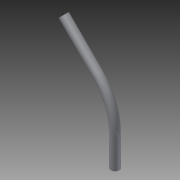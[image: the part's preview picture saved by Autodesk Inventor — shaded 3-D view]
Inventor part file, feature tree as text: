
AUTODESK INVENTOR PART (.ipt)
format: ipt  version: 2014 SP1 (Build 180222100, 222)  size: 117,248 bytes
history: native  units: in
note: dims shown in document units (in); Inventor stores cm internally (conversion verified against a paired STEP export)
features: reference x5, sketch x2, plane x2, sweep x1
ambient origin geometry x8: Origin, YZ Plane, XZ Plane, XY Plane, X Axis, Y Axis, Z Axis, Center Point
bodies: Solid1 (feature_tree)
feature tree (10):
  sketch  "Sketch1"  dims[d0=0.7274in d1=0.7274in]
  plane  "Work Plane2"
  sweep  "Sweep1"
  reference  "Reference1"
  reference  "Reference2"
  reference  "Reference3"
  reference  "Reference4"
  plane  "Work Plane1"
  sketch  "Sketch2"  dims[d2=0.5in d3=0.0in d4=0.45in]
  reference  "Reference5"
